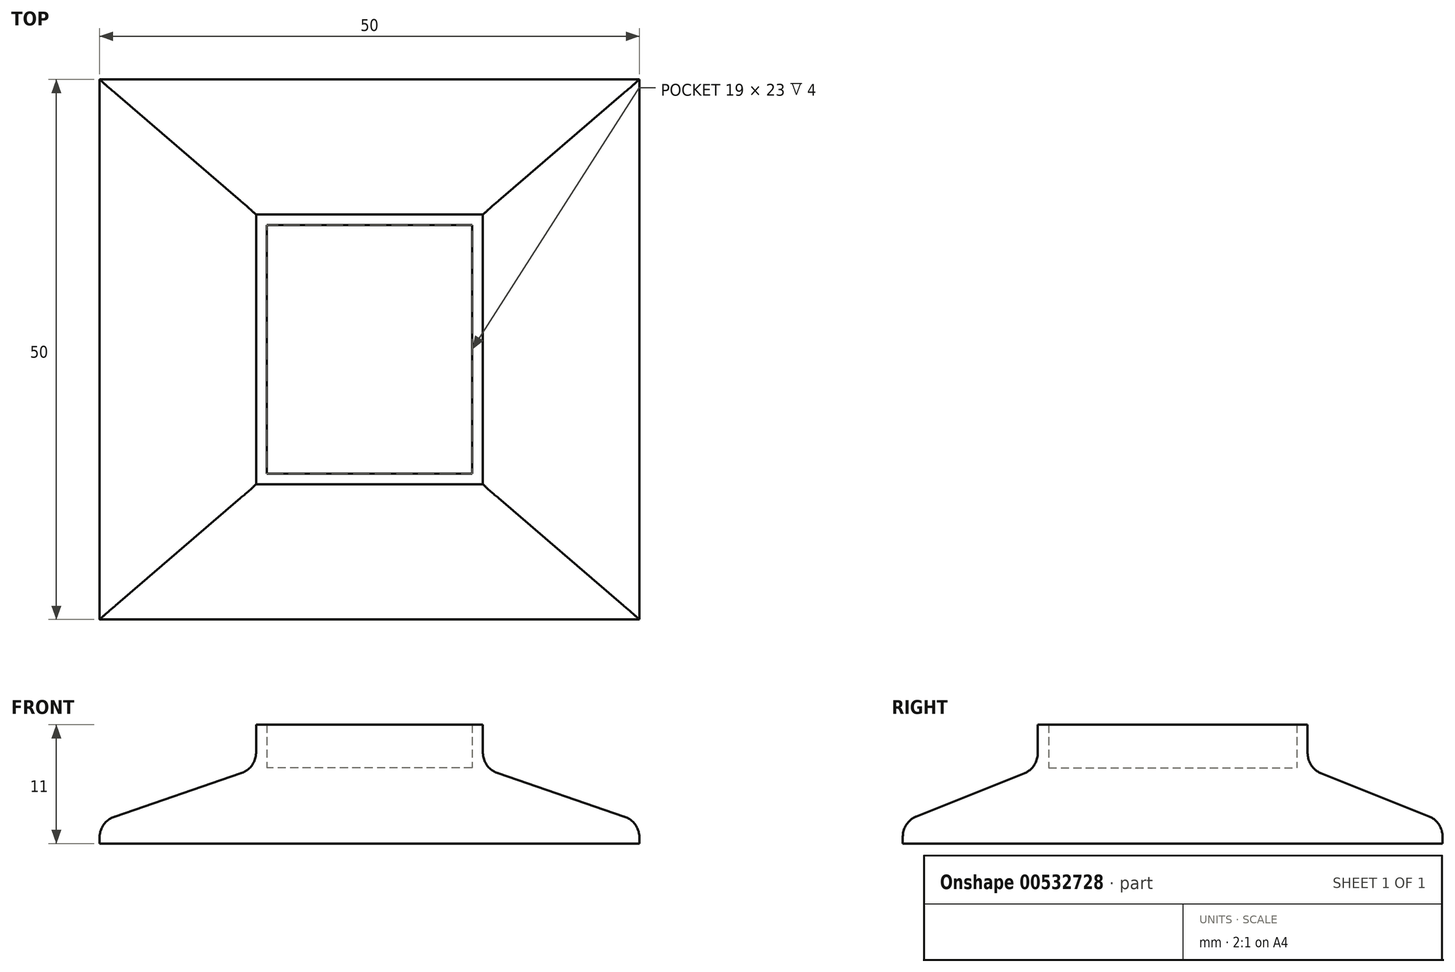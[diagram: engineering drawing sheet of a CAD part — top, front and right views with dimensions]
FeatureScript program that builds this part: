
annotation { "Feature Type Name" : "Feature", "Feature Type Description" : "" }
export const myFeature = defineFeature(function(context is Context, id is Id, definition is map)
    precondition{}
    {
        {
            var Q0;
            Q0=qCreatedBy(makeId("Top.planeOp"),FACE);
            var sketch = newSketch(context, id + "F0", { "sketchPlane" : qUnion([Q0])});
            skLineSegment(sketch, "E0.bottom", {"start": v(9.5, -11.5) * mm, "end": v(-9.5, -11.5) * mm, "construction": true});
            skLineSegment(sketch, "E0.top", {"start": v(9.5, 11.5) * mm, "end": v(-9.5, 11.5) * mm, "construction": true});
            skLineSegment(sketch, "E0.left", {"start": v(9.5, -11.5) * mm, "end": v(9.5, 11.5) * mm, "construction": true});
            skLineSegment(sketch, "E0.right", {"start": v(-9.5, -11.5) * mm, "end": v(-9.5, 11.5) * mm, "construction": true});
            skPoint(sketch, "E0.middle", {"position": v(0, 0) * mm});
            skLineSegment(sketch, "E1.bottom", {"start": v(-10.5, 12.5) * mm, "end": v(10.5, 12.5) * mm});
            skLineSegment(sketch, "E1.top", {"start": v(-10.5, -12.5) * mm, "end": v(10.5, -12.5) * mm});
            skLineSegment(sketch, "E1.left", {"start": v(-10.5, 12.5) * mm, "end": v(-10.5, -12.5) * mm});
            skLineSegment(sketch, "E1.right", {"start": v(10.5, 12.5) * mm, "end": v(10.5, -12.5) * mm});
            skSolve(sketch);
        }
        {
            var Q0;
            Q0=qCreatedBy(makeId("Top.planeOp"),FACE);
            cPlane(context, id + "F1", {"entities" : qUnion([Q0]), "cplaneType" : CPlaneType.OFFSET, "offset" : 5 * mm, "oppositeDirection" : true, "width" : 150 * mm, "height" : 150 * mm});
        }
        {
            var Q0;
            Q0=qCreatedBy(id+"F1.planeOp",FACE);
            var sketch = newSketch(context, id + "F2", { "sketchPlane" : qUnion([Q0])});
            skLineSegment(sketch, "E2.bottom", {"start": v(-25, 25) * mm, "end": v(25, 25) * mm});
            skLineSegment(sketch, "E2.top", {"start": v(-25, -25) * mm, "end": v(25, -25) * mm});
            skLineSegment(sketch, "E2.left", {"start": v(-25, 25) * mm, "end": v(-25, -25) * mm});
            skLineSegment(sketch, "E2.right", {"start": v(25, 25) * mm, "end": v(25, -25) * mm});
            skPoint(sketch, "E2.middle", {"position": v(0, 0) * mm});
            skSolve(sketch);
        }
        {
            var Q0;
            Q0=makeQuery(id+"F2.imprint","IMPRINT",FACE,{"disambiguationData":[TD([[makeQuery(id+"F2.imprint","IMPRINT",EDGE,{"derivedFrom":sQuery(id+"F2.wireOp",EDGE,"E2.bottom")}),-1.0]])]});
            var Q1;
            Q1=makeQuery(id+"F0.imprint","IMPRINT",FACE,{"disambiguationData":[TD([[makeQuery(id+"F0.imprint","IMPRINT",EDGE,{"derivedFrom":sQuery(id+"F0.wireOp",EDGE,"E1.bottom")}),-1.0]])]});
            loft(context, id + "F3", {"sheetProfilesArray" : [{ "sheetProfileEntities" : qUnion([Q0]) }, { "sheetProfileEntities" : qUnion([Q1]) }]});
        }
        {
            var Q0;
            Q0=makeQuery(id+"F3.opLoft","CAP_FACE",FACE,{"disambiguationData":[OSD([makeQuery(id+"F0.imprint","IMPRINT",FACE,{"disambiguationData":[TD([[makeQuery(id+"F0.imprint","IMPRINT",EDGE,{"derivedFrom":sQuery(id+"F0.wireOp",EDGE,"E1.bottom")}),-1.0]])]})])],"isStart":true});
            var sketch = newSketch(context, id + "F4", { "sketchPlane" : qUnion([Q0])});
            skLineSegment(sketch, "E3.bottom", {"start": v(10.5, -12.5) * mm, "end": v(-10.5, -12.5) * mm});
            skLineSegment(sketch, "E3.top", {"start": v(10.5, 12.5) * mm, "end": v(-10.5, 12.5) * mm});
            skLineSegment(sketch, "E3.left", {"start": v(10.5, -12.5) * mm, "end": v(10.5, 12.5) * mm});
            skLineSegment(sketch, "E3.right", {"start": v(-10.5, -12.5) * mm, "end": v(-10.5, 12.5) * mm});
            skPoint(sketch, "E3.middle", {"position": v(0, 0) * mm});
            skLineSegment(sketch, "E4.bottom", {"start": v(9.5, -11.5) * mm, "end": v(-9.5, -11.5) * mm});
            skLineSegment(sketch, "E4.top", {"start": v(9.5, 11.5) * mm, "end": v(-9.5, 11.5) * mm});
            skLineSegment(sketch, "E4.left", {"start": v(9.5, -11.5) * mm, "end": v(9.5, 11.5) * mm});
            skLineSegment(sketch, "E4.right", {"start": v(-9.5, -11.5) * mm, "end": v(-9.5, 11.5) * mm});
            skSolve(sketch);
        }
        {
            var Q0;
            Q0=makeQuery(id+"F4.imprint","IMPRINT",FACE,{"disambiguationData":[TD([[makeQuery(id+"F4.imprint","IMPRINT",EDGE,{"derivedFrom":sQuery(id+"F4.wireOp",EDGE,"E3.bottom")}),1.0]])]});
            extrude(context, id + "F5", {"entities" : qUnion([Q0]), "operationType" : NewBodyOperationType.ADD, "depth" : 4 * mm, "offsetDistance" : 25 * mm});
        }
        {
            var Q0;
            Q0=makeQuery(id+"F3.opLoft","CAP_FACE",FACE,{"disambiguationData":[OSD([makeQuery(id+"F2.imprint","IMPRINT",FACE,{"disambiguationData":[TD([[makeQuery(id+"F2.imprint","IMPRINT",EDGE,{"derivedFrom":sQuery(id+"F2.wireOp",EDGE,"E2.bottom")}),-1.0]])]})])],"isStart":true});
            extrude(context, id + "F6", {"entities" : qUnion([Q0]), "operationType" : NewBodyOperationType.ADD, "depth" : 2 * mm, "offsetDistance" : 25 * mm});
        }
        {
            var Q0;
            {var subQ0=sQuery(id+"F2.wireOp",EDGE,"E2.right");var subQ1=sQuery(id+"F2.wireOp",EDGE,"E2.top");var subQ2=sQuery(id+"F2.wireOp",EDGE,"E2.bottom");Q0=makeQuery(id+"F6.boolean.opBoolean","MERGE",EDGE,{"derivedFrom":[makeQuery(id+"F3.opLoft","MID_CAP_EDGE",EDGE,{"disambiguationData":[OSD([subQ2,subQ1,subQ0])],"capPos":0.0}),makeQuery(id+"F6.opExtrude","CAP_EDGE",EDGE,{"disambiguationData":[OSD([subQ2,subQ1,subQ0])],"isStart":true})]});}
            var Q1;
            {var subQ0=sQuery(id+"F2.wireOp",EDGE,"E2.right");var subQ1=sQuery(id+"F2.wireOp",EDGE,"E2.left");var subQ2=sQuery(id+"F2.wireOp",EDGE,"E2.top");Q1=makeQuery(id+"F6.boolean.opBoolean","MERGE",EDGE,{"derivedFrom":[makeQuery(id+"F3.opLoft","MID_CAP_EDGE",EDGE,{"disambiguationData":[OSD([subQ2,subQ1,subQ0])],"capPos":0.0}),makeQuery(id+"F6.opExtrude","CAP_EDGE",EDGE,{"disambiguationData":[OSD([subQ2,subQ1,subQ0])],"isStart":true})]});}
            var Q2;
            {var subQ0=sQuery(id+"F2.wireOp",EDGE,"E2.right");var subQ1=sQuery(id+"F2.wireOp",EDGE,"E2.left");var subQ2=sQuery(id+"F2.wireOp",EDGE,"E2.bottom");Q2=makeQuery(id+"F6.boolean.opBoolean","MERGE",EDGE,{"derivedFrom":[makeQuery(id+"F3.opLoft","MID_CAP_EDGE",EDGE,{"disambiguationData":[OSD([subQ2,subQ1,subQ0])],"capPos":0.0}),makeQuery(id+"F6.opExtrude","CAP_EDGE",EDGE,{"disambiguationData":[OSD([subQ2,subQ1,subQ0])],"isStart":true})]});}
            var Q3;
            {var subQ0=sQuery(id+"F2.wireOp",EDGE,"E2.left");var subQ1=sQuery(id+"F2.wireOp",EDGE,"E2.top");var subQ2=sQuery(id+"F2.wireOp",EDGE,"E2.bottom");Q3=makeQuery(id+"F6.boolean.opBoolean","MERGE",EDGE,{"derivedFrom":[makeQuery(id+"F3.opLoft","MID_CAP_EDGE",EDGE,{"disambiguationData":[OSD([subQ2,subQ1,subQ0])],"capPos":0.0}),makeQuery(id+"F6.opExtrude","CAP_EDGE",EDGE,{"disambiguationData":[OSD([subQ2,subQ1,subQ0])],"isStart":true})]});}
            var Q4;
            Q4=makeQuery(id+"F5.boolean.opBoolean","MERGE",EDGE,{"derivedFrom":[makeQuery(id+"F3.opLoft","MID_CAP_EDGE",EDGE,{"disambiguationData":[OSD([sQuery(id+"F0.wireOp",EDGE,"E1.bottom"),sQuery(id+"F0.wireOp",EDGE,"E1.left"),sQuery(id+"F0.wireOp",EDGE,"E1.right")])],"capPos":1.0}),makeQuery(id+"F5.opExtrude","CAP_EDGE",EDGE,{"disambiguationData":[OSD([sQuery(id+"F4.wireOp",EDGE,"E3.top")])],"isStart":true})]});
            var Q5;
            Q5=makeQuery(id+"F5.boolean.opBoolean","MERGE",EDGE,{"derivedFrom":[makeQuery(id+"F3.opLoft","MID_CAP_EDGE",EDGE,{"disambiguationData":[OSD([sQuery(id+"F0.wireOp",EDGE,"E1.bottom"),sQuery(id+"F0.wireOp",EDGE,"E1.top"),sQuery(id+"F0.wireOp",EDGE,"E1.left")])],"capPos":1.0}),makeQuery(id+"F5.opExtrude","CAP_EDGE",EDGE,{"disambiguationData":[OSD([sQuery(id+"F4.wireOp",EDGE,"E3.right")])],"isStart":true})]});
            var Q6;
            Q6=makeQuery(id+"F5.boolean.opBoolean","MERGE",EDGE,{"derivedFrom":[makeQuery(id+"F3.opLoft","MID_CAP_EDGE",EDGE,{"disambiguationData":[OSD([sQuery(id+"F0.wireOp",EDGE,"E1.top"),sQuery(id+"F0.wireOp",EDGE,"E1.left"),sQuery(id+"F0.wireOp",EDGE,"E1.right")])],"capPos":1.0}),makeQuery(id+"F5.opExtrude","CAP_EDGE",EDGE,{"disambiguationData":[OSD([sQuery(id+"F4.wireOp",EDGE,"E3.bottom")])],"isStart":true})]});
            var Q7;
            Q7=makeQuery(id+"F5.boolean.opBoolean","MERGE",EDGE,{"derivedFrom":[makeQuery(id+"F3.opLoft","MID_CAP_EDGE",EDGE,{"disambiguationData":[OSD([sQuery(id+"F0.wireOp",EDGE,"E1.bottom"),sQuery(id+"F0.wireOp",EDGE,"E1.top"),sQuery(id+"F0.wireOp",EDGE,"E1.right")])],"capPos":1.0}),makeQuery(id+"F5.opExtrude","CAP_EDGE",EDGE,{"disambiguationData":[OSD([sQuery(id+"F4.wireOp",EDGE,"E3.left")])],"isStart":true})]});
            fillet(context, id + "F7", {"entities" : qUnion([Q0, Q1, Q2, Q3, Q4, Q5, Q6, Q7]), "tangentPropagation" : true, "radius" : 2 * mm, "defaultsChanged" : false, "vertexSettings" : [], "allowEdgeOverflow" : false});
        }
    });
